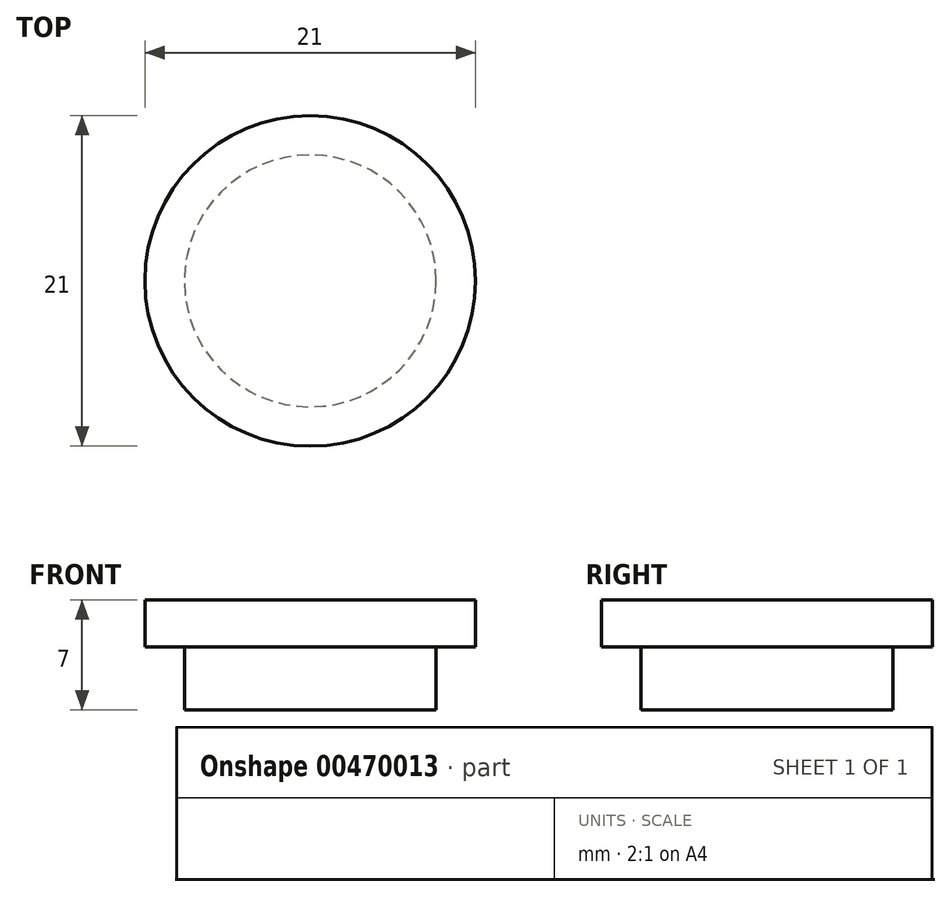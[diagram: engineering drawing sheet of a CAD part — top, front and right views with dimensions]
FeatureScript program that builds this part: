
annotation { "Feature Type Name" : "Feature", "Feature Type Description" : "" }
export const myFeature = defineFeature(function(context is Context, id is Id, definition is map)
    precondition{}
    {
        {
            var Q0;
            Q0=qCreatedBy(makeId("Top.planeOp"),FACE);
            var sketch = newSketch(context, id + "F0", { "sketchPlane" : qUnion([Q0])});
            skCircle(sketch, "E0", {"center": v(0, 0) * mm, "radius": 10.5 * mm});
            skCircle(sketch, "E1", {"center": v(0, 0) * mm, "radius": 8 * mm});
            skSolve(sketch);
        }
        {
            var Q0;
            Q0 = qSketchRegion(id + "F0", true);
            extrude(context, id + "F1", {"entities" : qUnion([Q0]), "oppositeDirection" : true, "depth" : 3 * mm, "offsetDistance" : 25 * mm});
        }
        {
            var Q0;
            Q0=makeQuery(id+"F0.imprint","IMPRINT",FACE,{"disambiguationData":[TD([[makeQuery(id+"F0.imprint","IMPRINT",EDGE,{"derivedFrom":sQuery(id+"F0.wireOp",EDGE,"E1")}),1.0]])]});
            extrude(context, id + "F2", {"entities" : qUnion([Q0]), "operationType" : NewBodyOperationType.ADD, "oppositeDirection" : true, "depth" : 7 * mm, "offsetDistance" : 25 * mm});
        }
    });
